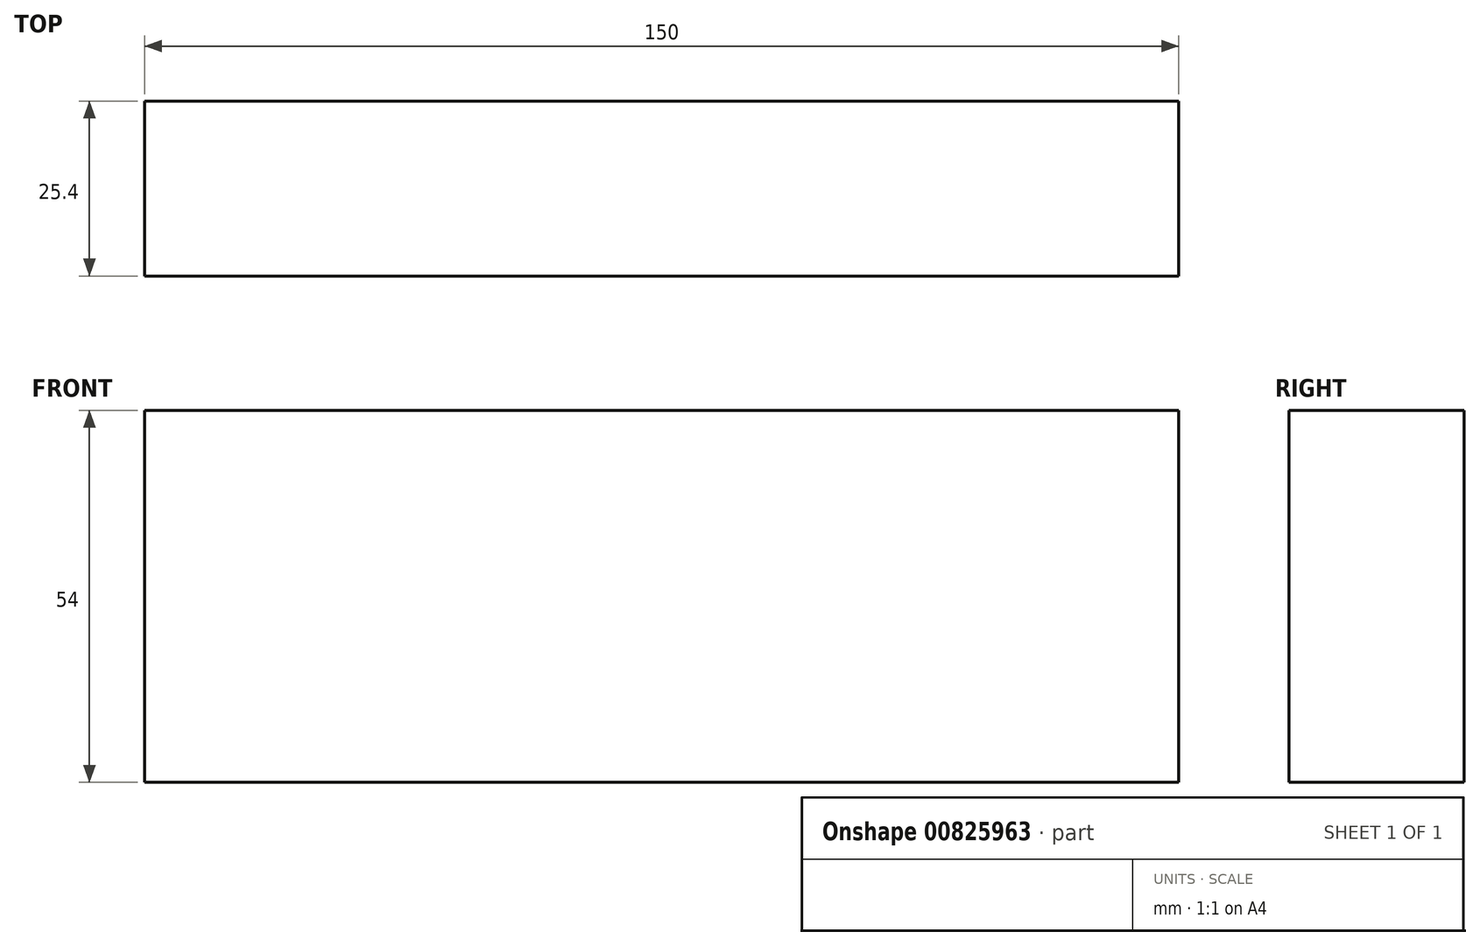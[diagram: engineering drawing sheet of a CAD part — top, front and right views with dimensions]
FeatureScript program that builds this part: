
annotation { "Feature Type Name" : "Feature", "Feature Type Description" : "" }
export const myFeature = defineFeature(function(context is Context, id is Id, definition is map)
    precondition{}
    {
        {
            var Q0;
            Q0=qCreatedBy(makeId("Front.planeOp"),FACE);
            var sketch = newSketch(context, id + "F0", { "sketchPlane" : qUnion([Q0])});
            skLineSegment(sketch, "E0.bottom", {"start": v(-75, 27) * mm, "end": v(75, 27) * mm});
            skLineSegment(sketch, "E0.top", {"start": v(-75, -27) * mm, "end": v(75, -27) * mm});
            skLineSegment(sketch, "E0.left", {"start": v(-75, 27) * mm, "end": v(-75, -27) * mm});
            skLineSegment(sketch, "E0.right", {"start": v(75, 27) * mm, "end": v(75, -27) * mm});
            skPoint(sketch, "E0.middle", {"position": v(0, 0) * mm});
            skSolve(sketch);
        }
        {
            var Q0;
            Q0 = qSketchRegion(id + "F0", true);
            extrude(context, id + "F1", {"entities" : qUnion([Q0]), "depth" : 25.4 * mm, "offsetDistance" : 25.4 * mm});
        }
    });
